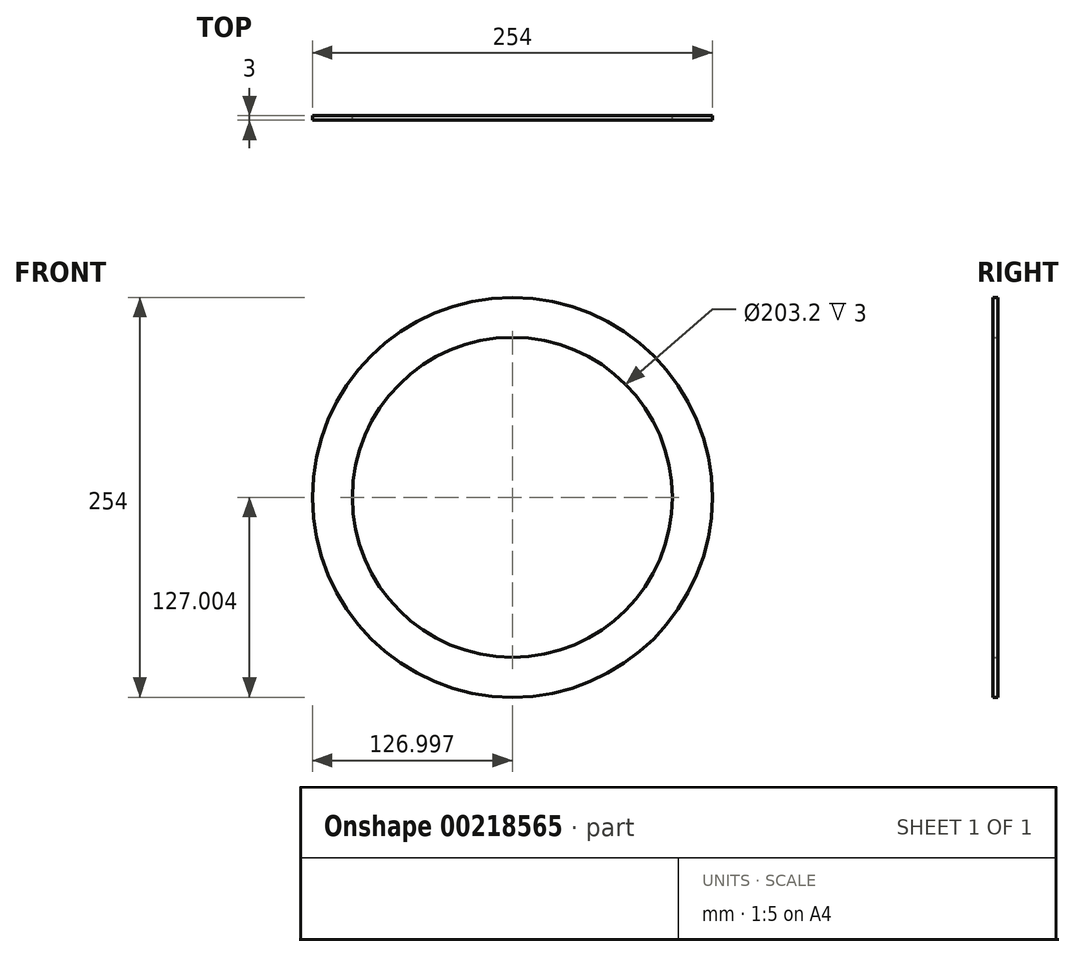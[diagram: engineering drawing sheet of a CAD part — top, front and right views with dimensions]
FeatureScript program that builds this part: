
annotation { "Feature Type Name" : "Feature", "Feature Type Description" : "" }
export const myFeature = defineFeature(function(context is Context, id is Id, definition is map)
    precondition{}
    {
        {
            var Q0;
            Q0=qCreatedBy(makeId("Front.planeOp"),FACE);
            var sketch = newSketch(context, id + "F0", { "sketchPlane" : qUnion([Q0])});
            skCircle(sketch, "E0", {"center": v(-18.1, 4.9) * mm, "radius": 101.6 * mm});
            skCircle(sketch, "E1", {"center": v(-18.1, 4.9) * mm, "radius": 127 * mm});
            skSolve(sketch);
        }
        {
            var Q0;
            Q0=makeQuery(id+"F0.imprint","IMPRINT",FACE,{"disambiguationData":[TD([[makeQuery(id+"F0.imprint","IMPRINT",EDGE,{"derivedFrom":sQuery(id+"F0.wireOp",EDGE,"E0")}),-1.0]])]});
            extrude(context, id + "F1", {"entities" : qUnion([Q0]), "depth" : 3 * mm});
        }
    });
